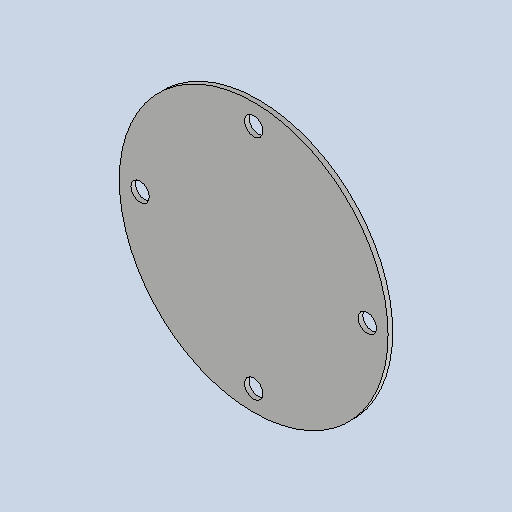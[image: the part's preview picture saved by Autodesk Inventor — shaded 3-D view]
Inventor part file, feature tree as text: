
AUTODESK INVENTOR PART (.ipt)
format: ipt  version: 2025 (Build 290162010, 162A)  size: 113,664 bytes
history: native  units: mm
features: sketch x2, sheet_metal_op x1, extrude x1, pattern_circular x1, other x1
ambient origin geometry x8: Origin, YZ Plane, XZ Plane, XY Plane, X Axis, Y Axis, Z Axis, Center Point
bodies: Solid1 (feature_tree)
feature tree (6):
  sheet_metal_op  "Face1"
  extrude  "Extrusion1"  Depth=3.0mm
  pattern_circular  "Circular Pattern1"  Count=8  [1 undecoded]
  sketch  "Sketch1"  dims[d0=175.0mm d1=3.0mm d2=80.0mm]
  other  "Plate1"
  sketch  "Sketch2"  dims[d3=80.0mm d8=0.0mm d9=0.0mm d10=40.0mm d11=360.0deg d16=12.0mm d17=13.5mm d18=0.5mm d19=0.872665mm d20=0.5mm d21=0.872665mm]
note: 1 required parameter value undecoded (feature->parameter linkage not recoverable at this tier; creation-order binding heuristic only, values carry confidence <= 0.55)
